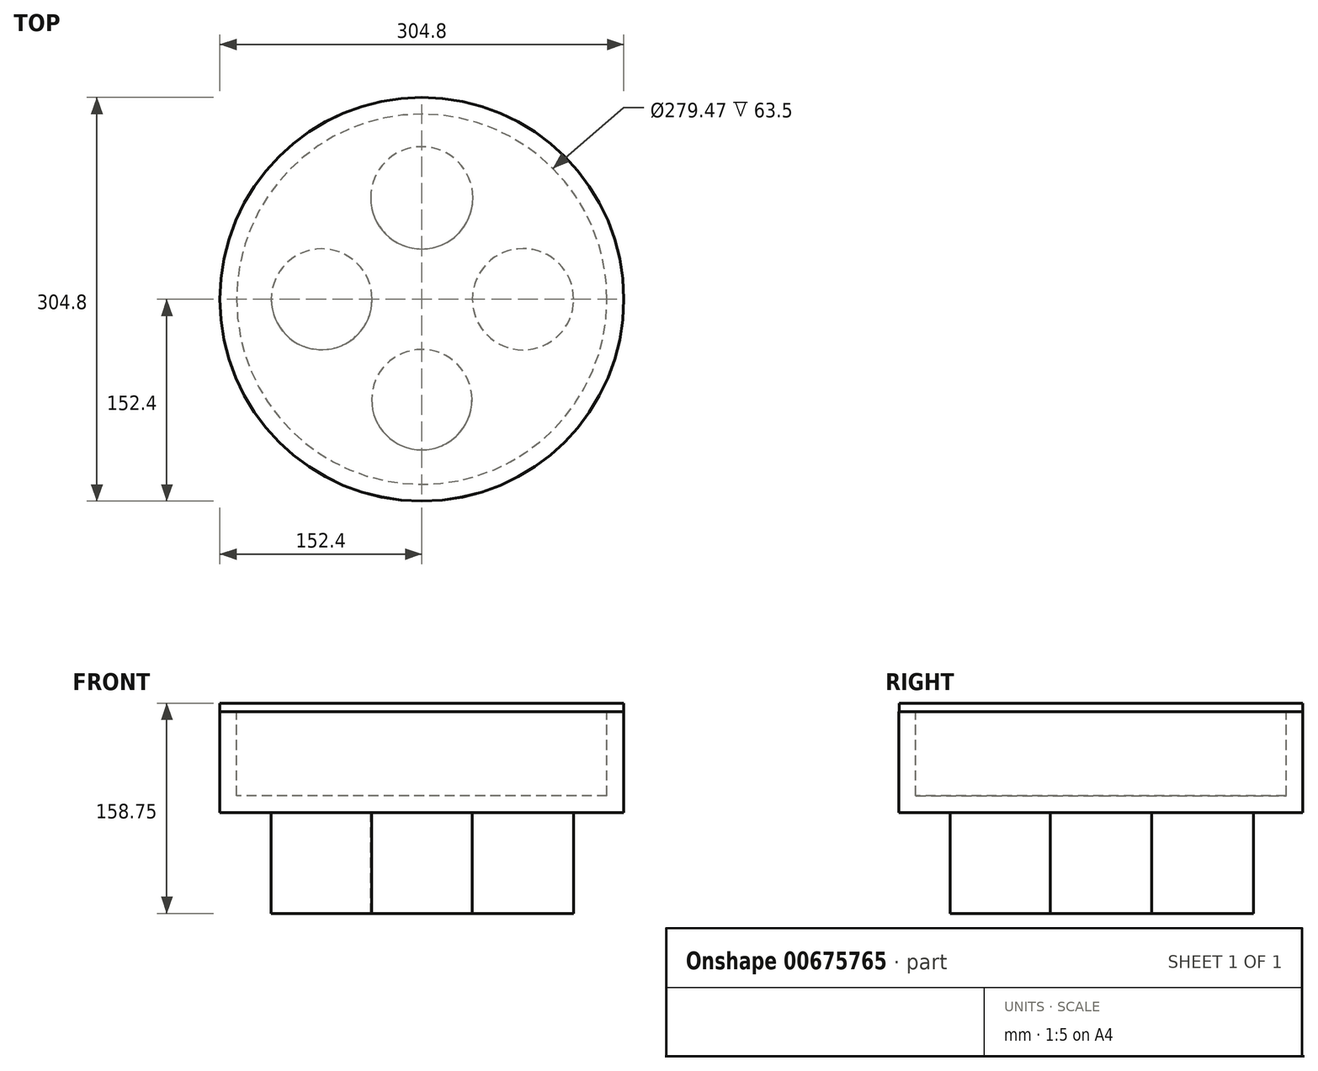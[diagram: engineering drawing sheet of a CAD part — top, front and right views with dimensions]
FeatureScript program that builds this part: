
annotation { "Feature Type Name" : "Feature", "Feature Type Description" : "" }
export const myFeature = defineFeature(function(context is Context, id is Id, definition is map)
    precondition{}
    {
        {
            var Q0;
            Q0=qCreatedBy(makeId("Top.planeOp"),FACE);
            var sketch = newSketch(context, id + "F0", { "sketchPlane" : qUnion([Q0])});
            skCircle(sketch, "E0", {"center": v(0, 0) * mm, "radius": 152.4 * mm});
            skSolve(sketch);
        }
        {
            var Q0;
            Q0=makeQuery(id+"F0.imprint","IMPRINT",FACE,{"disambiguationData":[TD([[makeQuery(id+"F0.imprint","IMPRINT",EDGE,{"derivedFrom":sQuery(id+"F0.wireOp",EDGE,"E0")}),1.0]])]});
            extrude(context, id + "F1", {"entities" : qUnion([Q0]), "depth" : 76.2 * mm, "offsetDistance" : 25.4 * mm});
        }
        {
            var Q0;
            Q0=makeQuery(id+"F1.opExtrude","CAP_FACE",FACE,{"disambiguationData":[OSD([sQuery(id+"F0.wireOp",EDGE,"E0")])],"isStart":false});
            var sketch = newSketch(context, id + "F2", { "sketchPlane" : qUnion([Q0])});
            skCircle(sketch, "E1", {"center": v(0, 0) * mm, "radius": 139.74 * mm});
            skSolve(sketch);
        }
        {
            var Q0;
            Q0 = qSketchRegion(id + "F2", true);
            extrude(context, id + "F3", {"entities" : qUnion([Q0]), "operationType" : NewBodyOperationType.REMOVE, "oppositeDirection" : true, "depth" : 63.5 * mm, "offsetDistance" : 25.4 * mm});
        }
        {
            var Q0;
            Q0=makeQuery(id+"F1.opExtrude","CAP_FACE",FACE,{"disambiguationData":[OSD([sQuery(id+"F0.wireOp",EDGE,"E0")])],"isStart":false});
            var sketch = newSketch(context, id + "F4", { "sketchPlane" : qUnion([Q0])});
            skCircle(sketch, "E2", {"center": v(0, 0) * mm, "radius": 152.4 * mm});
            skSolve(sketch);
        }
        {
            var Q0;
            Q0 = qSketchRegion(id + "F4", true);
            extrude(context, id + "F5", {"entities" : qUnion([Q0]), "depth" : 6.35 * mm, "offsetDistance" : 25.4 * mm});
        }
        {
            var Q0;
            Q0=makeQuery(id+"F1.opExtrude","CAP_FACE",FACE,{"disambiguationData":[OSD([sQuery(id+"F0.wireOp",EDGE,"E0")])],"isStart":true});
            var sketch = newSketch(context, id + "F6", { "sketchPlane" : qUnion([Q0])});
            skCircle(sketch, "E3", {"center": v(76.33, 0) * mm, "radius": 38.22 * mm});
            skCircle(sketch, "E4", {"center": v(0, 75.82) * mm, "radius": 37.88 * mm});
            skCircle(sketch, "E5", {"center": v(-75.57, 0) * mm, "radius": 38.05 * mm});
            skCircle(sketch, "E6", {"center": v(0, -76.58) * mm, "radius": 38.6 * mm});
            skSolve(sketch);
        }
        {
            var Q0;
            Q0 = qSketchRegion(id + "F6", true);
            extrude(context, id + "F7", {"entities" : qUnion([Q0]), "operationType" : NewBodyOperationType.ADD, "depth" : 76.2 * mm, "offsetDistance" : 25.4 * mm});
        }
    });
